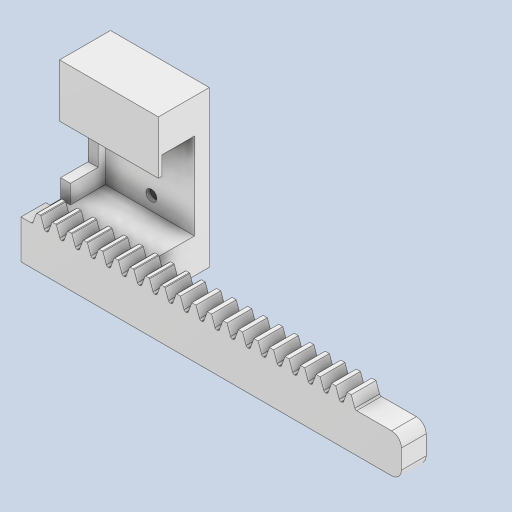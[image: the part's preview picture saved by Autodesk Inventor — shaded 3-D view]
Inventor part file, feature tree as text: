
AUTODESK INVENTOR PART (.ipt)
format: ipt  version: 2023 (Build 270158000, 158)  size: 379,904 bytes
history: native  units: mm
features: extrude x6, sketch x6, pattern_linear x1, chamfer x1, hole x1, fillet x1
ambient origin geometry x8: Origin, YZ Plane, XZ Plane, XY Plane, X Axis, Y Axis, Z Axis, Center Point
bodies: Solid1 (feature_tree)
feature tree (16):
  extrude  "Extrusion1"  Depth=10.0mm TaperAngle=0.0deg
  extrude  "Extrusion2"  Depth=10.0mm TaperAngle=0.0deg
  pattern_linear  "Rectangular Pattern1"  Spacing1=0.1mm  [1 undecoded]
  chamfer  "面取り1"  Distance=10.125mm
  extrude  "押し出し7"  Depth=75.0mm
  extrude  "押し出し10"  Depth=17.5mm
  hole  "穴1"  [1 undecoded]
  extrude  "押し出し11"  Depth=7.0mm
  extrude  "押し出し12"  Depth=3.0mm
  fillet  "フィレット1"  Radius=10.75mm
  sketch  "Sketch_1"  dims[d0=5.0mm d1=0.0mm d2=10.0mm d3=0.0mm d4=220.0mm d6=3.142mm d7=10.0mm d9=0.0mm d10=0.1mm d11=2.0mm d12=45.0deg d13=10.125mm d14=75.0mm d37=17.5mm d41=7.0mm d42=7.0mm d43=3.0mm d44=10.75mm d58=18.0mm d59=0.0mm d76=2.8mm d78=10.0mm d79=3.0mm d80=2.0mm d81=0.0mm d88=12.0mm d89=6.0mm d90=9.3mm d91=9.3mm d92=2.2mm d93=6.0mm d94=5.0mm d95=2.2mm d96=90.0deg d97=8.0mm d98=20.594885mm d99=1.5mm d100=9.6mm d101=18.1mm d102=4.5mm d103=4.0mm d104=10.0mm d105=10.0mm d107=10.0mm d108=20.0mm d110=23.5mm d113=6.0mm d114=0.0mm d115=5.0mm d116=0.0mm d117=2.0mm]
  sketch  "スケッチ5"
  sketch  "スケッチ9"
  sketch  "スケッチ10"
  sketch  "スケッチ11"
  sketch  "スケッチ12"
note: 2 required parameter values undecoded (feature->parameter linkage not recoverable at this tier; creation-order binding heuristic only, values carry confidence <= 0.55)
